# Revit family: AD-S12 - X Mount
name_source: partatom
category: Generic Models
revit_build: Autodesk Revit Architecture 2012 (Build: 20110309_2315(x64)
units: mm (PartAtom-declared; Revit-internal decimal feet)

## types (1)
- AD-S12 - X Mount
    Coverage Horizontal = 75.00°
    Coverage Vertical = 75.00°
    Default Elevation = 0' - 0"
    Depth = 1' - 0 23/32"
    Description = 12" 2-Way Surface Mount Loudspeaker
    Height = 1' - 11 15/32"
    Impedance = 8
    Manufacturer = QSC Audio Products, LLC
    Manufacturer URL = www.qscaudio.com
    Model = AD-S12
    Mount Depth = 0' - 1"
    Mount Height = 0' - 5 9/32"
    Mount Width = 0' - 4 11/32"
    Power Handling = 300
    Product Documentation Link = TBA
    Product Page URL = TBA
    Regulatory Compliance = RoHS
    SPL Max = 126
    Sensitivity = 95
    URL = TBA
    Weight Dimensional (kg) = 21
    Weight Dimensional (lb) = 46.3
    Weight Product (kg) = 16
    Weight Product (lb) = 35
    Width = 1' - 1 15/16"

## geometry (parser evidence)
native form markers: Sweep x12
no freeform markers — native parametric forms only
